# Revit family: PRD_FrankeWS_WshTrghs_SaturnWashTrough_PREL214,321_PRES212,318
name_source: partatom
category: Plumbing Fixtures
revit_build: Autodesk Revit 2018 (Build: 20190510_1515(x64)
units: mm (PartAtom-declared; Revit-internal decimal feet)

## family parameters
Cut with Voids When Loaded = No
Host = Face
OmniClass Number = 23.45.05.14.14
OmniClass Title = Sinks/Lavatories
Part Type = Normal
Room Calculation Point = No
Round Connector Dimension = Use Diameter
Shared = No

## types (4) — shared parameters
AssetType = Fixed
Category = Pr_40_20_96_99, Wash troughs
Color = Stainless steel
Default Elevation = 850 mm  [stored 2.78871 ft]
DrainSize = DN 40 (1 1/2 inch.)
DurationUnit = year
Finish = Satin finished
Form = Wall mounted
IfcExportAs = IfcSanitaryTerminalType
IfcExportType = WASHHANDBASIN
IntegralAccessories = Bracket, stainless steel screws and dowels included
Manufacturer = KWC Group AG
ManufacturerName = KWC Group AG
ManufacturerURL = www.kwc.com
Material = Stainless steel
MaterialsBody = Stainless steel 1.4301
MaterialsFinishAndColour = Stainless steel, satin finished
NBSDescription = Wash troughs
NBSReference = 45-35-70/370
NominalDepth = 570 mm  [stored 1.87008 ft]
NominalHeight = 150 mm
OutletSize = DN 40 (1 1/2 inch.)
ProductInformation = https://pim.kwc.com
Shape = Rectangular
URL = www.kwc.com
Uniclass2015Code = Pr_40_20_96_99
Uniclass2015Title = Wash troughs
Uniclass2015Version = Products v1.10
Version = 1
WarrantyDurationUnit = year
WashHandBasinMounting = WallHung
WashHandBasinType = WashingTrough
WashbasinMaterial = PRD_AR_StainlessSteel_SatinFinished
WasteSize = 40  [stored 0.131234 ft]
WaterSupplyOverflowAndWasteHolesOverflow = None
WaterSupplyOverflowAndWasteHolesWaste = Center-Front
WaterSupplyOverflowAndWasteHolesWaterSupply = No tapholes

## per-type parameters (varying)
| type | BIMObjectName | Description | Features | GrossWeight | Model | ModelNumber | ModelReference | Name | NetWeight | NominalWidth | Size | Stations | Type |
| PREL214, Width=1400 | PRD_AR_WashTrough_SaturnWashTrough_PREL214 | Wash trough PRESTIGE, for wall mounting in single-row, stainless steel, surface satin finished, material thickness 1.2 mm, with G 1 1/2 B flat perforated waste, with bracket, stainless steel screws and dowels included. length 1400 , with 2 wash places | stainless steel, 1.20 mm, satin finished, wall mounting, 1400x150x570 mm (WxHxD) | 21.90 kg | PREL214 | 2000100787 | PREL214 | SATURN wash trough PREL214 | 19.00 kg | 1400 mm  [stored 4.59318 ft] | 1400 x 570 x 150 mm | 2 | prel |
| PREL321, Width=2100 | PRD_AR_WashTrough_SaturnWashTrough_PREL321 | Wash trough PRESTIGE, for wall mounting in single-row, stainless steel, surface satin finished, material thickness 1.2 mm, with G 1 1/2 B flat perforated waste, with bracket, stainless steel screws and dowels included. length 2100 mm, with 3 wash places | stainless steel, 1.20 mm, satin finished, wall mounting, 2100x150x570 mm (WxHxD) | 28.20 kg | PREL321 | 2000100789 | PREL321 | SATURN wash trough PREL321 | 24.50 kg | 2100 mm | 2100 x 570 x 150 mm | 3 | prel |
| PRES212, Width=1200 | PRD_AR_WashTrough_SaturnWashTrough_PRES212 | Wash trough PRESTIGE, for wall mounting in single-row, stainless steel, surface satin finished, material thickness 1.2 mm, with G 1 1/2 B flat perforated waste, with bracket, stainless steel screws and dowels included. length 1200 mm, with 2 wash places | stainless steel, 1.20 mm, satin finished, wall mounting, 1200x150x570 mm (WxHxD) | 18.40 kg | PRES212 | 2000100790 | PRES212 | SATURN wash trough PRES212 | 16.00 kg | 1200 mm  [stored 3.93701 ft] | 1200 x 570 x 150 mm | 2 | pres |
| PRES318, Width=1800 | PRD_AR_WashTrough_SaturnWashTrough_PRES318 | Wash trough PRESTIGE, for wall mounting in single-row, stainless steel, surface satin finished, material thickness 1.2 mm, with G 1 1/2 B flat perforated waste, with bracket, stainless steel screws and dowels included. length 1800 mm, with 3 wash places | stainless steel, 1.20 mm, satin finished, wall mounting, 1800x150x570 mm (WxHxD) | 24.70 kg | PRES318 | 2000100791 | PRES318 | SATURN wash trough PRES318 | 21.50 kg | 1800 mm  [stored 5.90551 ft] | 1800 x 570 x 150 mm | 3 | pres |

note: [stored X ft] marks values corroborated as IEEE doubles in the binary element streams (Revit-internal decimal feet)

## geometry (parser evidence)
native form markers: Sweep x7
no freeform markers — native parametric forms only
